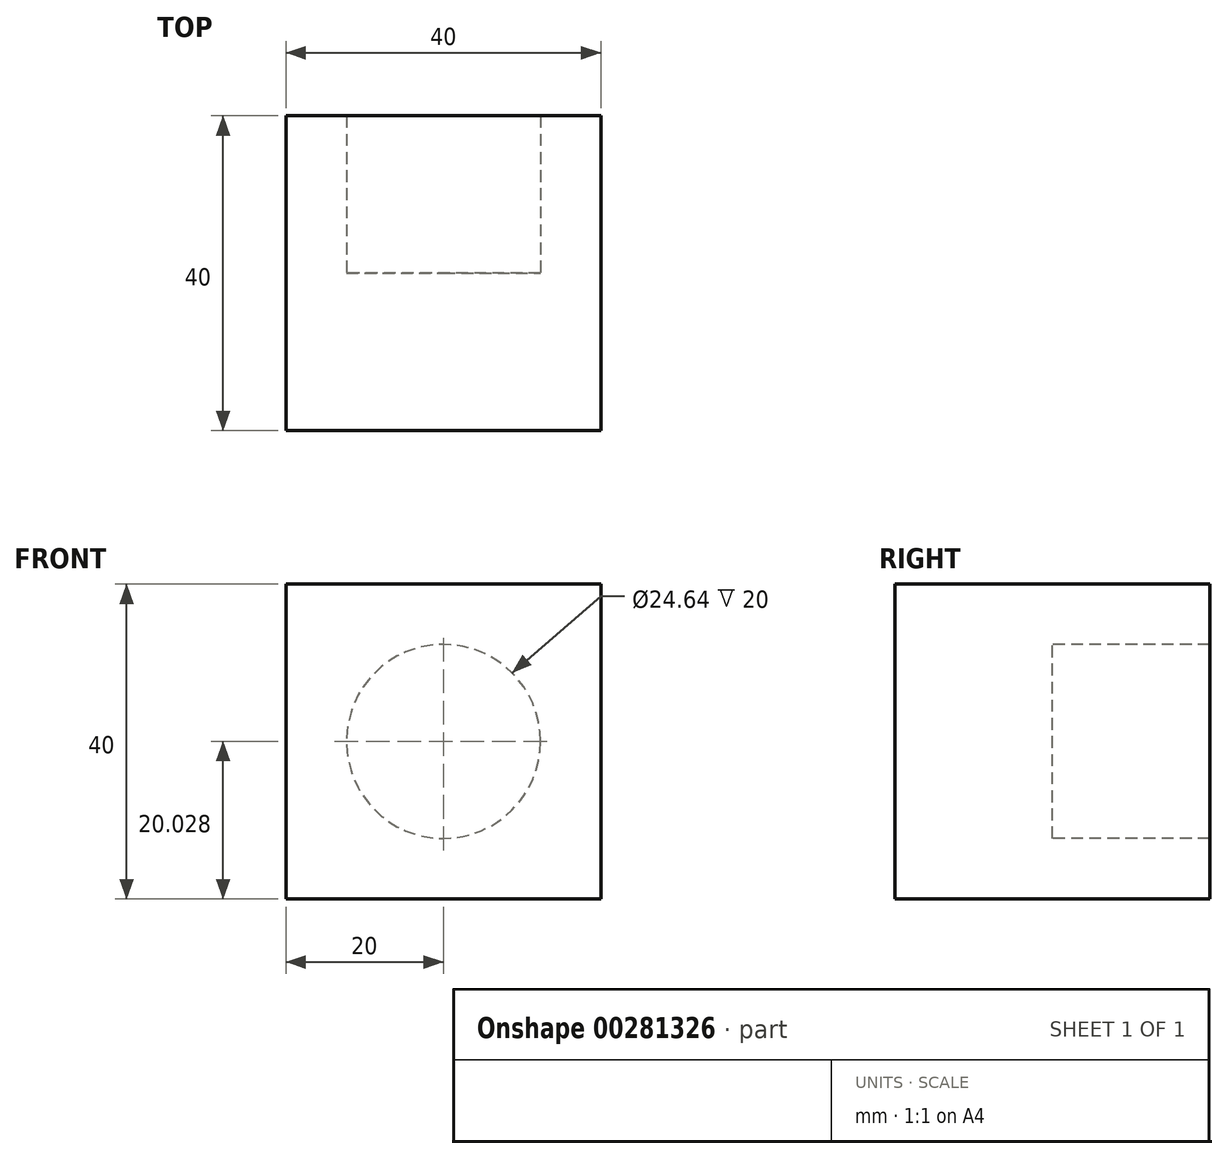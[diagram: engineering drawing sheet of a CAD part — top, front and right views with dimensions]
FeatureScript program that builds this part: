
annotation { "Feature Type Name" : "Feature", "Feature Type Description" : "" }
export const myFeature = defineFeature(function(context is Context, id is Id, definition is map)
    precondition{}
    {
        {
            var Q0;
            Q0=qCreatedBy(makeId("Top.planeOp"),FACE);
            var sketch = newSketch(context, id + "F0", { "sketchPlane" : qUnion([Q0])});
            skLineSegment(sketch, "E0.bottom", {"start": v(-20, -20) * mm, "end": v(20, -20) * mm});
            skLineSegment(sketch, "E0.top", {"start": v(-20, 20) * mm, "end": v(20, 20) * mm});
            skLineSegment(sketch, "E0.left", {"start": v(-20, -20) * mm, "end": v(-20, 20) * mm});
            skLineSegment(sketch, "E0.right", {"start": v(20, -20) * mm, "end": v(20, 20) * mm});
            skPoint(sketch, "E0.middle", {"position": v(0, 0) * mm});
            skSolve(sketch);
        }
        {
            var Q0;
            Q0 = qSketchRegion(id + "F0", true);
            extrude(context, id + "F1", {"entities" : qUnion([Q0]), "depth" : 40 * mm});
        }
        {
            var Q0;
            Q0=qCreatedBy(makeId("Front.planeOp"),FACE);
            var sketch = newSketch(context, id + "F2", { "sketchPlane" : qUnion([Q0])});
            skCircle(sketch, "E1", {"center": v(0, 20.03) * mm, "radius": 12.32 * mm});
            skSolve(sketch);
        }
        {
            var Q0;
            Q0 = qSketchRegion(id + "F2", true);
            extrude(context, id + "F3", {"entities" : qUnion([Q0]), "operationType" : NewBodyOperationType.REMOVE, "oppositeDirection" : true, "depth" : 20 * mm});
        }
    });
